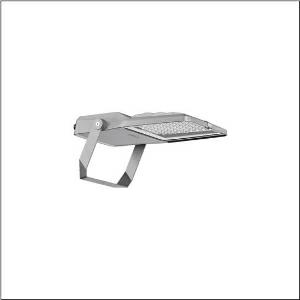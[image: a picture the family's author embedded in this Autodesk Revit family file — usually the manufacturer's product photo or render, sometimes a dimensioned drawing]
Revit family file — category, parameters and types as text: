
# Revit family: floodlight_fl_21_mini___pl64_5xa7775b2e1a_35e6
name_source: partatom
category: Lighting Fixtures
units: mm (PartAtom-declared; Revit-internal decimal feet)

## family parameters
Cut with Voids When Loaded = No
Host = Face
Light Source = No
Part Type = Normal
Room Calculation Point = No
Round Connector Dimension = Use Diameter
Shared = No

## types (1)
- --- (1 x LED, 6010 lm, 45.7 W, 3000K)
    Apparent Load = 46 VA
    CIE Flux Codes = 28 80 98 100 100
    Color Rendering = 70
    Color Temperature = 3000K
    Default Elevation = 1800 mm
    Description = Floodlight FL 21 mini, floodlight, primary light control with lens, of PMMA, primary optical cover: protective disc, of toughened safety glass, transparent, light distribution: PL64, light emission: direct distribution, installation type: surface-mounted, LED, High Power LED, rated luminous flux: 6.010lm, luminous efficacy: 132lm/W, light colour: 730, colour temperature: 3000K, control gear: ECG Smart Interface, control: flexible luminous flux parameterisation, time-dependent luminous flux control, constant luminous flux control, overheat protection, presetting dimming logarithmic, with terminal, 6-pole, mains connection: 220..240V, AC, 50/60Hz, start of lifetime: 46W, end of lifetime: 48W, reduction: 22W, luminaire housing, of diecast aluminium, powder-coated, Siteco® metallic grey (DB 702S), corrosivity category C5 according to DIN EN ISO 12944, mounting bracket, of steel, galvanised, powder-coated, Siteco® metallic grey (DB 702S), protection rating (complete): IP66, insulation class (complete): insulation class II (safety insulation), certification: CE, ENEC, VDE, protection symbol: D, impact resistance: IK08, permissible operating ambient temperature: -40..+40°C, permissible operating ambient temperature for outdoor applications: -40..+50°C, standard: DIN EN 12944, packaging unit: 1 piece

Light Distribution: PL64
    Height = 70 mm
    Lamp = 1 x LED
    Lamp Light Flux = 6010 lm
    Lamp Power = 45.7 W
    Lamp count = 1
    Length = 485 mm
    Luminous efficacy = 132 lm/W
    Manufacturer = Siteco
    ModVariant = No
    Model = 5XA7775B2E1A
    Number of Poles = 1
    OnlyDefault = Yes
    Power Factor = 1
    Product Name = Floodlight FL 21 mini | PL64
    Product group = floodlight | pylon top
    ProductGroupID = 6101
    Protection Class = Protection class II
    Protection Degree = IP 66
    RLX_Detail_Level = 1
    RlxData = <blob elided: 95789 chars, md5=6a0fb09f>
    Socket = socket
    Standby Power = 0 W
    System Light Flux = 6010 lm
    System Power = 46 W
    Type Comments = factory setting: luminous flux: 100 % | dim-lin: 254 | 463 mA
    Type Image = l_1006845.jpg
    URL = http://relux.com
    VarID = @adj_076629
    Voltage = 0 V
    Weight = 0.00 kg
    Width = 337 mm

## geometry (parser evidence)
native form markers: Blend x4, Sweep x13
no freeform markers — native parametric forms only
